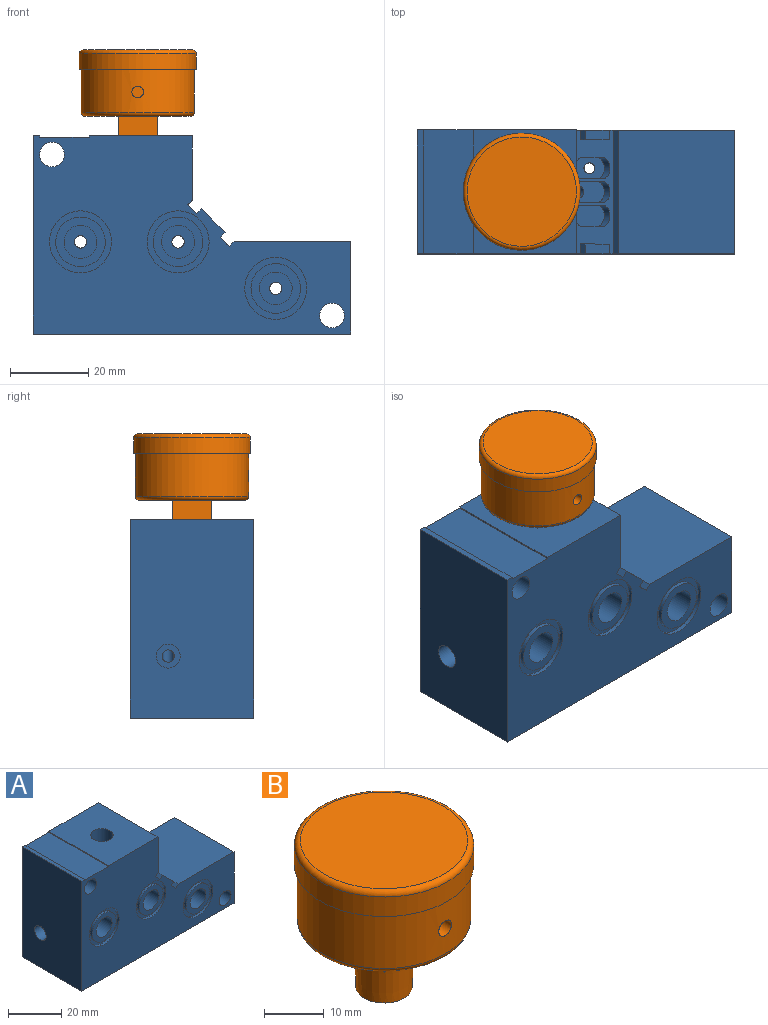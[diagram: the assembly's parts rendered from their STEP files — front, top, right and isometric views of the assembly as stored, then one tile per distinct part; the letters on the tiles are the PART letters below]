
ASSEMBLY  parts=2 mates=1
PART A: 99 faces, bbox 81.9x32.3x51.4 mm
  f0: plane 31.75x26.48mm, normal (0,0,1), area 784.9mm2, adj f1,f92,f95,f96,f97
  f1: plane 31.75x16.38mm, normal (1,0,0), area 519.9mm2, adj f0,f2,f86,f87,f89,f90,f92,f96
  f2: plane 4.32x1.45mm, normal (0.71,0,-0.71), area 6.5mm2, adj f1,f3,f90,f92
  f3: plane 32.22x11.13mm, normal (0.71,0,0.71), area 240.6mm2, adj f2,f4,f16,f17,f18,f19,f21,f22
  f4: plane 6.56x6.56mm, normal (0,-1,0), area 14.7mm2, adj f3,f5,f16,f18
  f5: plane 8.98x8.98mm, normal (0.71,0,0.71), area 56.9mm2, adj f4,f6,f16,f17,f18
  f6: cylinder r=1.38mm len=5.99mm, axis (0.71,0,0.71), area 45.3mm2, adj f5,f7
  f7: cylinder r=1.59mm len=12.7mm, axis (0,-1,0), area 119.8mm2, adj f6,f8,f14
  f8: plane 8.43x8.43mm, normal (0,-1,0), area 47.9mm2, adj f7,f9
  f9: cylinder r=4.22mm len=9.53mm, axis (0,-1,0), area 252.3mm2, adj f8,f10
  f10: plane 12.7x12.7mm, normal (0,-1,0), area 70.8mm2, adj f9,f11
  f11: cylinder r=6.35mm len=12.7mm, axis (0,-1,0), area 40.5mm2, adj f10,f12
  f12: plane 15.88x15.88mm, normal (0,-1,0), area 71.3mm2, adj f11,f13
  f13: cylinder r=7.94mm len=15.88mm, axis (0,-1,0), area 50.7mm2, adj f12,f92
  f14: plane 8.43x8.43mm, normal (0,1,0), area 47.9mm2, adj f7,f15
  f15: cylinder r=4.22mm len=9.53mm, axis (0,1,0), area 252.3mm2, adj f14,f96
  f16: cylinder r=2.73mm len=5.46mm, axis (0.71,0,0.71), area 17.4mm2, adj f3,f4,f5,f17
  f17: plane 6.56x6.56mm, normal (0,1,0), area 14.7mm2, adj f3,f5,f16,f18
  f18: cylinder r=2.73mm len=5.46mm, axis (0.71,0,0.71), area 17.4mm2, adj f3,f4,f5,f17
  f19: plane 2.54x1.26mm, normal (-0.71,0,0.71), area 4.5mm2, adj f3,f20,f21,f96
  f20: plane 6.11x6.11mm, normal (0.71,0,0.71), area 21.9mm2, adj f19,f21,f22,f96
  f21: plane 7.36x7.36mm, normal (0,-1,0), area 15.4mm2, adj f3,f19,f20,f22
  f22: plane 2.54x1.26mm, normal (0.71,0,-0.71), area 4.5mm2, adj f3,f20,f21,f96
  f23: plane 31.75x1.26mm, normal (-0.71,0,0.71), area 56.5mm2, adj f3,f24,f92,f96
  f24: plane 31.75x29.85mm, normal (0,0,1), area 947.6mm2, adj f23,f25,f92,f96
  f25: plane 31.75x23.75mm, normal (1,0,0), area 754mm2, adj f24,f26,f92,f96
  f26: plane 81.28x31.75mm, normal (0,0,-1), area 2413.1mm2, adj f25,f27,f44,f56,f57,f92,f96
  f27: plane 50.8x31.75mm, normal (-1,0,0), area 1583.2mm2, adj f26,f28,f31,f92,f96
  f28: plane 31.75x1.59mm, normal (0,0,1), area 50.4mm2, adj f27,f29,f92,f96
  f29: plane 31.75x0.38mm, normal (1,0,0), area 12.1mm2, adj f28,f30,f92,f96
  f30: plane 31.75x12.7mm, normal (0,0,1), area 403.2mm2, adj f29,f92,f95,f96
  f31: cylinder r=3.07mm len=6.35mm, axis (-1,0,0), area 122.6mm2, adj f27,f32
  f32: plane 6.15x6.15mm, normal (-1,0,0), area 21.8mm2, adj f31,f33
  f33: cylinder r=1.59mm len=20.4mm, axis (-1,0,0), area 193.4mm2, adj f32,f34,f41
  f34: cylinder r=1.59mm len=3.18mm, axis (0,1,0), area 8.7mm2, adj f33,f35,f97
  f35: cylinder r=1.59mm len=17.2mm, axis (-1,0,0), area 157.2mm2, adj f34,f36,f37,f38,f41
  f36: cone r=0mm half-angle=59deg, axis (-1,0,0), area 0mm2, adj f35,f38
  f37: cone r=0mm half-angle=59deg, axis (-1,0,0), area 0mm2, adj f35,f38
  f38: cylinder r=1.38mm len=17.59mm, axis (0,0,-1), area 130.9mm2, adj f35,f36,f37,f39,f40
  f39: plane 8.43x8.43mm, normal (0,0,-1), area 49.8mm2, adj f38,f56
  f40: plane 9.56x9.56mm, normal (0.71,0,0.71), area 54.4mm2, adj f38,f77,f78,f79,f80
  f41: cylinder r=1.59mm len=3.43mm, axis (0,1,0), area 24.1mm2, adj f33,f35,f42
  f42: plane 6.15x6.15mm, normal (0,1,0), area 21.8mm2, adj f41,f43
  f43: cylinder r=3.07mm len=6.35mm, axis (0,1,0), area 122.6mm2, adj f42,f96
  f44: cylinder r=4.22mm len=9.53mm, axis (0,0,-1), area 252.3mm2, adj f26,f45
  f45: plane 8.43x8.43mm, normal (0,0,-1), area 47.9mm2, adj f44,f46
  f46: cylinder r=1.59mm len=14.1mm, axis (0,0,-1), area 132.7mm2, adj f45,f47
  f47: cylinder r=1.59mm len=12.7mm, axis (0,-1,0), area 118.8mm2, adj f46,f48,f50
  f48: plane 8.43x8.43mm, normal (0,1,0), area 47.9mm2, adj f47,f49
  f49: cylinder r=4.22mm len=9.53mm, axis (0,1,0), area 252.3mm2, adj f48,f96
  f50: plane 8.43x8.43mm, normal (0,-1,0), area 47.9mm2, adj f47,f51
  f51: cylinder r=4.22mm len=9.53mm, axis (0,-1,0), area 252.3mm2, adj f50,f52
  f52: plane 12.7x12.7mm, normal (0,-1,0), area 70.8mm2, adj f51,f53
  f53: cylinder r=6.35mm len=12.7mm, axis (0,-1,0), area 40.5mm2, adj f52,f54
  f54: plane 15.88x15.88mm, normal (0,-1,0), area 71.3mm2, adj f53,f55
  f55: cylinder r=7.94mm len=15.88mm, axis (0,-1,0), area 50.7mm2, adj f54,f92
  f56: cylinder r=4.22mm len=9.53mm, axis (0,0,-1), area 252.3mm2, adj f26,f39
  f57: cylinder r=4.22mm len=9.53mm, axis (0,0,-1), area 252.3mm2, adj f26,f58
  f58: plane 8.43x8.43mm, normal (0,0,-1), area 47.9mm2, adj f57,f59
  f59: cylinder r=1.59mm len=3.18mm, axis (0,0,-1), area 13.6mm2, adj f58,f60
  f60: cylinder r=1.59mm len=12.7mm, axis (0,-1,0), area 116.5mm2, adj f59,f61,f63,f69,f70,f71,f72
  f61: plane 8.43x8.43mm, normal (0,1,0), area 47.9mm2, adj f60,f62
  f62: cylinder r=4.22mm len=9.53mm, axis (0,1,0), area 252.3mm2, adj f61,f96
  f63: plane 8.43x8.43mm, normal (0,-1,0), area 47.9mm2, adj f60,f64
  f64: cylinder r=4.22mm len=9.53mm, axis (0,-1,0), area 252.3mm2, adj f63,f65
  f65: plane 12.7x12.7mm, normal (0,-1,0), area 70.8mm2, adj f64,f66
  f66: cylinder r=6.35mm len=12.7mm, axis (0,-1,0), area 40.5mm2, adj f65,f67
  f67: plane 15.88x15.88mm, normal (0,-1,0), area 71.3mm2, adj f66,f68
  f68: cylinder r=7.94mm len=15.88mm, axis (0,-1,0), area 50.7mm2, adj f67,f92
  f69: cone r=0mm half-angle=59deg, axis (0,0,-1), area 0mm2, adj f60,f70
  f70: cylinder r=1.59mm len=0.41mm, axis (0,0,-1), area 0mm2, adj f60,f69
  f71: cone r=0mm half-angle=59deg, axis (0,0,-1), area 0mm2, adj f60,f72
  f72: cylinder r=1.59mm len=0.41mm, axis (0,0,-1), area 0mm2, adj f60,f71
  f73: plane 2.54x1.26mm, normal (0.71,0,-0.71), area 4.5mm2, adj f3,f74,f75,f92
  f74: plane 6.11x6.11mm, normal (0.71,0,0.71), area 21.9mm2, adj f73,f75,f76,f92
  f75: plane 7.36x7.36mm, normal (0,1,0), area 15.4mm2, adj f3,f73,f74,f76
  f76: plane 2.54x1.26mm, normal (-0.71,0,0.71), area 4.5mm2, adj f3,f74,f75,f92
  f77: plane 6.56x6.56mm, normal (0,1,0), area 14.7mm2, adj f3,f40,f78,f80
  f78: cylinder r=2.73mm len=5.46mm, axis (0.71,0,0.71), area 17.4mm2, adj f3,f40,f77,f79
  f79: plane 6.56x6.56mm, normal (0,-1,0), area 14.7mm2, adj f3,f40,f78,f80
  f80: cylinder r=2.73mm len=5.46mm, axis (0.71,0,0.71), area 17.4mm2, adj f3,f40,f77,f79
  f81: plane 6.56x6.56mm, normal (0,1,0), area 14.7mm2, adj f3,f82,f83,f85
  f82: plane 8.98x8.98mm, normal (0.71,0,0.71), area 63mm2, adj f81,f83,f84,f85
  f83: cylinder r=2.73mm len=5.46mm, axis (0.71,0,0.71), area 17.4mm2, adj f3,f81,f82,f84
  f84: plane 6.56x6.56mm, normal (0,-1,0), area 14.7mm2, adj f3,f82,f83,f85
  f85: cylinder r=2.73mm len=5.46mm, axis (0.71,0,0.71), area 17.4mm2, adj f3,f81,f82,f84
  f86: plane 4.32x1.45mm, normal (0.71,0,-0.71), area 6.5mm2, adj f1,f3,f87,f96
  f87: cylinder r=1.25mm len=14.2mm, axis (1,0,0), area 107.1mm2, adj f1,f3,f86,f88,f89
  f88: cone r=0mm half-angle=59deg, axis (1,0,0), area 5.7mm2, adj f87
  f89: plane 21.16x1.45mm, normal (0.71,0,-0.71), area 35.6mm2, adj f1,f3,f87,f90
  f90: cylinder r=1.25mm len=14.2mm, axis (1,0,0), area 107.1mm2, adj f1,f2,f3,f89,f91
  f91: cone r=0mm half-angle=59deg, axis (1,0,0), area 5.7mm2, adj f90
  f92: plane 81.28x50.8mm, normal (0,-1,0), area 2416.6mm2, adj f0,f1,f2,f3,f13,f23,f24,f25
  f93: cylinder r=3.17mm len=31.75mm, axis (0,-1,0), area 633.4mm2, adj f92,f96
  f94: cylinder r=3.17mm len=31.75mm, axis (0,-1,0), area 633.4mm2, adj f92,f96
  f95: plane 31.75x0.38mm, normal (-1,0,0), area 12.1mm2, adj f0,f30,f92,f96
  f96: plane 81.28x50.8mm, normal (0,1,0), area 2813.1mm2, adj f0,f1,f3,f15,f19,f20,f22,f23
  f97: cylinder r=4.22mm len=38.1mm, axis (0,0,1), area 1001.3mm2, adj f0,f34,f98
  f98: cone r=0mm half-angle=59deg, axis (0,0,1), area 65.2mm2, adj f97
PART B: 19 faces, bbox 32.5x32.5x30 mm
  f0: cylinder r=1.5mm len=14.5mm, axis (0,1,0), area 136.7mm2, adj f4,f18
  f1: cone r=4.7mm half-angle=2.1deg, axis (0,0,1), area 244mm2, adj f6,f7,f8,f9,f17
  f2: torus R=14mm, axis (0,0,1), area 144.5mm2, adj f5,f12
  f3: torus R=13.5mm, axis (0,0,1), area 139.5mm2, adj f4,f10
  f4: cylinder r=14.5mm len=29mm, axis (0,0,1), area 995.1mm2, adj f0,f3,f11
  f5: cylinder r=15mm len=30mm, axis (0,0,1), area 377mm2, adj f2,f11
  f6: plane 5x5mm, normal (0,0,-1), area 5.4mm2, adj f1,f13,f14
  f7: plane 5x5mm, normal (0,0,-1), area 5.4mm2, adj f1,f13,f16
  f8: plane 5x5mm, normal (0,0,-1), area 5.4mm2, adj f1,f15,f16
  f9: plane 5x5mm, normal (0,0,-1), area 5.4mm2, adj f1,f14,f15
  f10: plane 27x27mm, normal (0,0,-1), area 472.6mm2, adj f3,f13,f14,f15,f16
  f11: plane 30x30mm, normal (0,0,-1), area 46.3mm2, adj f4,f5
  f12: plane 28x28mm, normal (0,0,1), area 615.8mm2, adj f2
  f13: plane 10x5mm, normal (1,0,0), area 50mm2, adj f6,f7,f10,f14,f16
  f14: plane 10x5mm, normal (0,-1,0), area 50mm2, adj f6,f9,f10,f13,f15
  f15: plane 10x5mm, normal (-1,0,0), area 50mm2, adj f8,f9,f10,f14,f16
  f16: plane 10x5mm, normal (0,1,0), area 50mm2, adj f7,f8,f10,f13,f15
  f17: plane 9.4x9.4mm, normal (0,0,-1), area 69.4mm2, adj f1
  f18: plane 3x3mm, normal (0,-1,0), area 7.1mm2, adj f0
PLACE A at identity
PLACE B t=(26.73,0,72.8)mm
MATE fastened B.f1 <-> A.f97  axis (0,0,-1) through (26.73,0,50.8)mm
